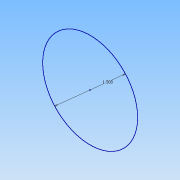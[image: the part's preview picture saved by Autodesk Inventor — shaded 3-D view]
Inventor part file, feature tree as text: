
AUTODESK INVENTOR PART (.ipt)
format: ipt  version: 2015 (Build 190159000, 159)  size: 57,856 bytes
history: native  units: in
note: dims shown in document units (in); Inventor stores cm internally (conversion verified against a paired STEP export)
features: sketch x1
ambient origin geometry x8: Origin, YZ Plane, XZ Plane, XY Plane, X Axis, Y Axis, Z Axis, Center Point
feature tree (1):
  sketch  "Sketch1"  dims[d0=1.5in]
